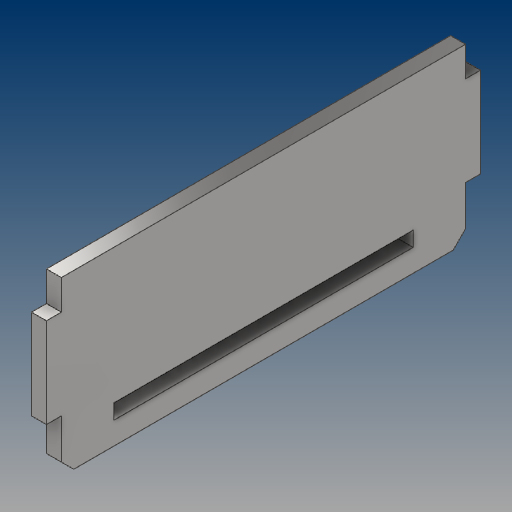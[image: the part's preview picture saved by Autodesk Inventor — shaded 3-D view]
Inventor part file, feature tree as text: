
AUTODESK INVENTOR PART (.ipt)
format: ipt  version: 2021 (Build 250183000, 183)  size: 154,112 bytes
history: native  units: mm
features: extrude x3, sketch x3, projected_geometry x2, chamfer x1
ambient origin geometry x8: Origin, YZ Plane, XZ Plane, XY Plane, X Axis, Y Axis, Z Axis, Center Point
bodies: Solid1 (feature_tree)
feature tree (9):
  extrude  "Extrusion1"  Depth=270.0mm
  extrude  "Extrusion2"  Depth=10.0mm TaperAngle=0.0deg
  extrude  "Extrusion3"  Depth=10.0mm
  chamfer  "Chamfer1"  Distance=60.0mm
  sketch  "Sketch1"  dims[d0=90.0mm d1=270.0mm]
  sketch  "Sketch2"  dims[d2=10.0mm d3=0.0mm d6=10.0mm d7=0.0mm]
  projected_geometry  "Projected Loop1"
  sketch  "Sketch3"  dims[d8=90.0mm d9=50.0mm d10=60.0mm d11=290.0mm d12=270.0mm d13=25.0mm d14=200.0mm d15=10.0mm d16=10.0mm d17=0.0mm d18=8.25mm d19=2.0mm d20=45.0deg]
  projected_geometry  "Projected Loop2"
